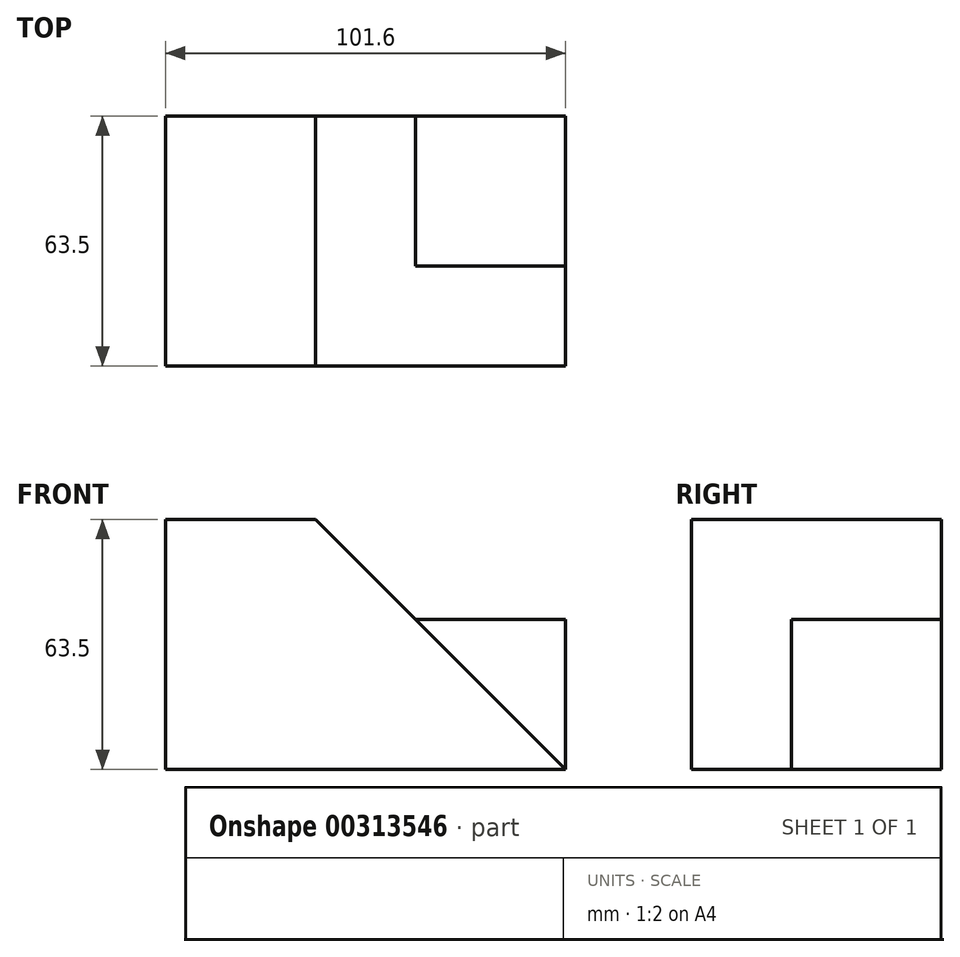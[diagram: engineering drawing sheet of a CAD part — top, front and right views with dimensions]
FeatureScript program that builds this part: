
annotation { "Feature Type Name" : "Feature", "Feature Type Description" : "" }
export const myFeature = defineFeature(function(context is Context, id is Id, definition is map)
    precondition{}
    {
        {
            var Q0;
            Q0=qCreatedBy(makeId("Front.planeOp"),FACE);
            var sketch = newSketch(context, id + "F0", { "sketchPlane" : qUnion([Q0])});
            skLineSegment(sketch, "E0", {"start": v(-33.1, -45.45) * mm, "end": v(-33.1, 18.05) * mm});
            skLineSegment(sketch, "E1", {"start": v(-33.1, 18.05) * mm, "end": v(5, 18.05) * mm});
            skLineSegment(sketch, "E2", {"start": v(-33.1, -45.45) * mm, "end": v(68.5, -45.45) * mm});
            skLineSegment(sketch, "E3", {"start": v(5, 18.05) * mm, "end": v(68.5, -45.45) * mm});
            skSolve(sketch);
        }
        {
            var Q0;
            Q0 = qSketchRegion(id + "F0", true);
            extrude(context, id + "F1", {"entities" : qUnion([Q0]), "depth" : 63.5 * mm});
        }
        {
            var Q0;
            Q0=makeQuery(id+"F1.opExtrude","CAP_FACE",FACE,{"disambiguationData":[OSD([sQuery(id+"F0.wireOp",EDGE,"E0"),sQuery(id+"F0.wireOp",EDGE,"E1"),sQuery(id+"F0.wireOp",EDGE,"E2"),sQuery(id+"F0.wireOp",EDGE,"E3")])],"isStart":true});
            var sketch = newSketch(context, id + "F2", { "sketchPlane" : qUnion([Q0])});
            skLineSegment(sketch, "E4", {"start": v(-68.5, -45.45) * mm, "end": v(-68.5, -7.35) * mm});
            skLineSegment(sketch, "E5", {"start": v(-68.5, -7.35) * mm, "end": v(-30.4, -7.35) * mm});
            skSolve(sketch);
        }
        {
            var Q0;
            Q0 = qSketchRegion(id + "F2", true);
            var Q1;
            {var subQ0=sQuery(id+"F2.wireOp",EDGE,"E4");Q1=makeQuery(id+"F2.imprint","IMPRINT",FACE,{"disambiguationData":[TD([[makeQuery(id+"F2.imprint","IMPRINT",EDGE,{"derivedFrom":subQ0}),-1.0]])]});}
            extrude(context, id + "F3", {"entities" : qUnion([Q0, Q1]), "oppositeDirection" : true, "depth" : 38.1 * mm});
        }
    });
